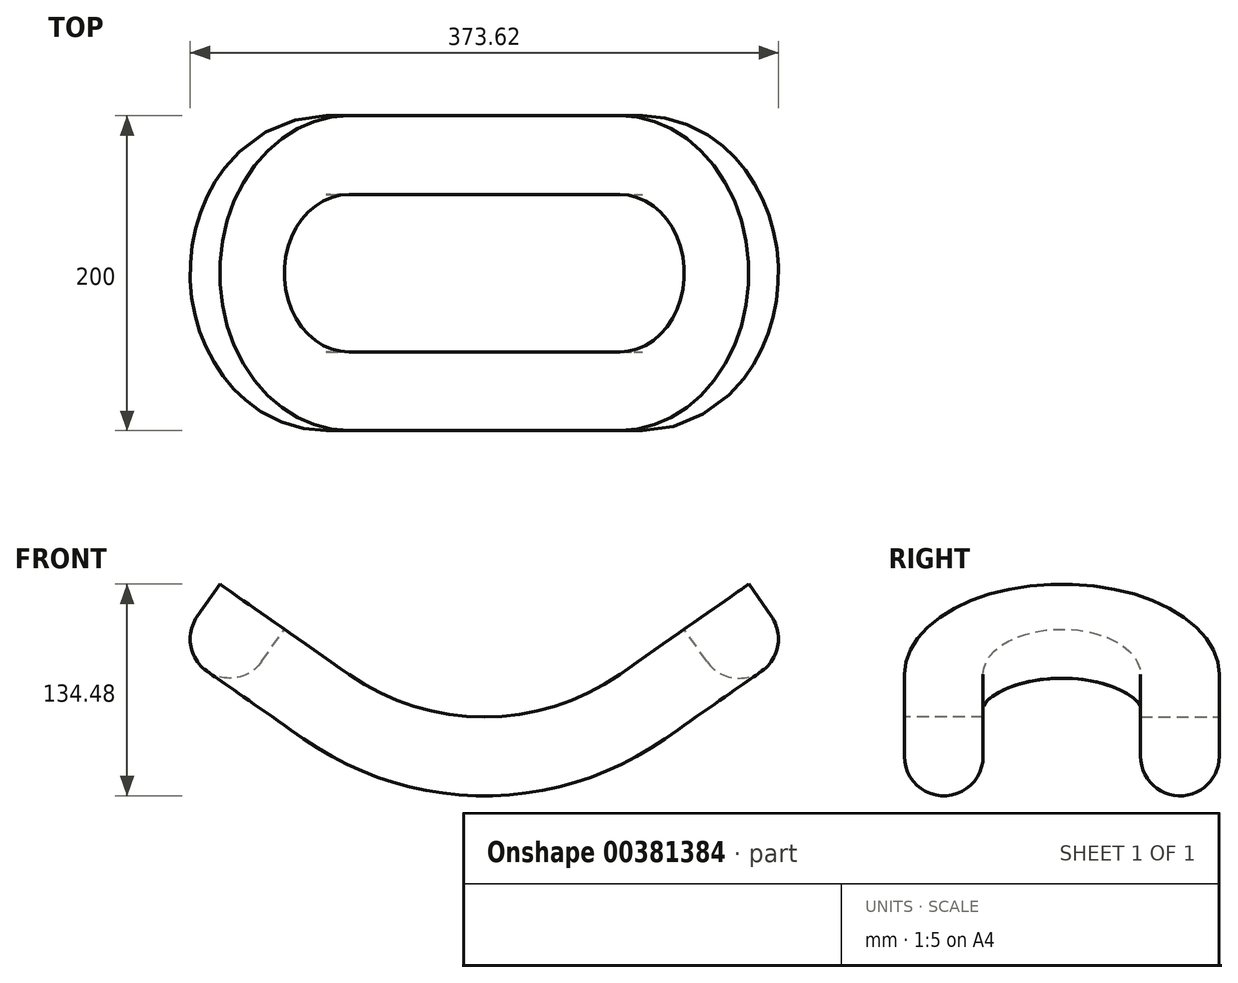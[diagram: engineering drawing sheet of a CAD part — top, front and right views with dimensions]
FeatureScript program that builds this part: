
annotation { "Feature Type Name" : "Feature", "Feature Type Description" : "" }
export const myFeature = defineFeature(function(context is Context, id is Id, definition is map)
    precondition{}
    {
        {
            var Q0;
            Q0=qCreatedBy(makeId("Front.planeOp"),FACE);
            var sketch = newSketch(context, id + "F0", { "sketchPlane" : qUnion([Q0])});
            skArc(sketch, "E0", {"start": v(0, 0) * mm, "mid": v(45.1, 6.94) * mm, "end": v(86.04, 27.13) * mm});
            skLineSegment(sketch, "E1", {"start": v(86.04, 27.13) * mm, "end": v(167.95, 84.48) * mm});
            skLineSegment(sketch, "E2", {"start": v(0, 150) * mm, "end": v(86.04, 27.13) * mm, "construction": true});
            skSolve(sketch);
        }
        {
            var Q0;
            Q0=sQuery(id+"F0.wireOp",EDGE,"E0");
            var Q1;
            Q1=sQuery(id+"F0.wireOp",EDGE,"E1");
            extrude(context, id + "F1", {"bodyType" : ToolBodyType.SURFACE, "surfaceEntities" : qUnion([Q0, Q1]), "depth" : 100 * mm});
        }
        {
            var Q0;
            Q0=makeQuery(id+"F1.opExtrude","SWEPT_FACE",FACE,{"disambiguationData":[OSD([sQuery(id+"F0.wireOp",EDGE,"E1")])]});
            var sketch = newSketch(context, id + "F2", { "sketchPlane" : qUnion([Q0])});
            skArc(sketch, "E3", {"start": v(186.04, 0) * mm, "mid": v(156.75, 70.71) * mm, "end": v(86.04, 100) * mm});
            skSolve(sketch);
        }
        {
            var Q0;
            Q0=qCreatedBy(makeId("Right.planeOp"),FACE);
            var sketch = newSketch(context, id + "F3", { "sketchPlane" : qUnion([Q0])});
            skLineSegment(sketch, "E4.bottom", {"start": v(-100, 0) * mm, "end": v(-50, 0) * mm});
            skLineSegment(sketch, "E4.top", {"start": v(-100, -25) * mm, "end": v(-50, -25) * mm, "construction": true});
            skLineSegment(sketch, "E4.left", {"start": v(-100, 0) * mm, "end": v(-100, -25) * mm});
            skLineSegment(sketch, "E4.right", {"start": v(-50, 0) * mm, "end": v(-50, -25) * mm});
            skArc(sketch, "E5", {"start": v(-50, -25) * mm, "mid": v(-75, -50) * mm, "end": v(-100, -25) * mm});
            skSolve(sketch);
        }
        {
            var Q0;
            Q0=makeQuery(id+"F3.imprint","IMPRINT",FACE,{"disambiguationData":[TD([[makeQuery(id+"F3.imprint","IMPRINT",EDGE,{"derivedFrom":sQuery(id+"F3.wireOp",EDGE,"E4.bottom")}),-1.0]])]});
            var Q1;
            Q1=makeQuery(id+"F1.opExtrude","CAP_EDGE",EDGE,{"disambiguationData":[OSD([sQuery(id+"F0.wireOp",EDGE,"E0")])],"isStart":false});
            var Q2;
            Q2=sQuery(id+"F2.wireOp",EDGE,"E3");
            sweep(context, id + "F4", {"profiles" : qUnion([Q0]), "path" : qUnion([Q1, Q2])});
        }
        {
            var Q0;
            Q0=makeQuery(id+"F4.opSweep","SWEPT_BODY",BODY,{"disambiguationData":[OSD([sQuery(id+"F2.wireOp",EDGE,"E3"),sQuery(id+"F3.wireOp",EDGE,"E4.bottom"),sQuery(id+"F3.wireOp",EDGE,"E4.left"),sQuery(id+"F3.wireOp",EDGE,"E4.right"),sQuery(id+"F3.wireOp",EDGE,"E5")])]});
            var Q1;
            Q1=qCreatedBy(makeId("Front.planeOp"),FACE);
            mirror(context, id + "F5", {"operationType" : NewBodyOperationType.ADD, "entities" : qUnion([Q0]), "mirrorPlane" : qUnion([Q1])});
        }
        {
            var Q0;
            Q0=makeQuery(id+"F4.opSweep","SWEPT_BODY",BODY,{"disambiguationData":[OSD([sQuery(id+"F2.wireOp",EDGE,"E3"),sQuery(id+"F3.wireOp",EDGE,"E4.bottom"),sQuery(id+"F3.wireOp",EDGE,"E4.left"),sQuery(id+"F3.wireOp",EDGE,"E4.right"),sQuery(id+"F3.wireOp",EDGE,"E5")])]});
            var Q1;
            Q1=qCreatedBy(makeId("Right.planeOp"),FACE);
            mirror(context, id + "F6", {"operationType" : NewBodyOperationType.ADD, "entities" : qUnion([Q0]), "mirrorPlane" : qUnion([Q1])});
        }
    });
